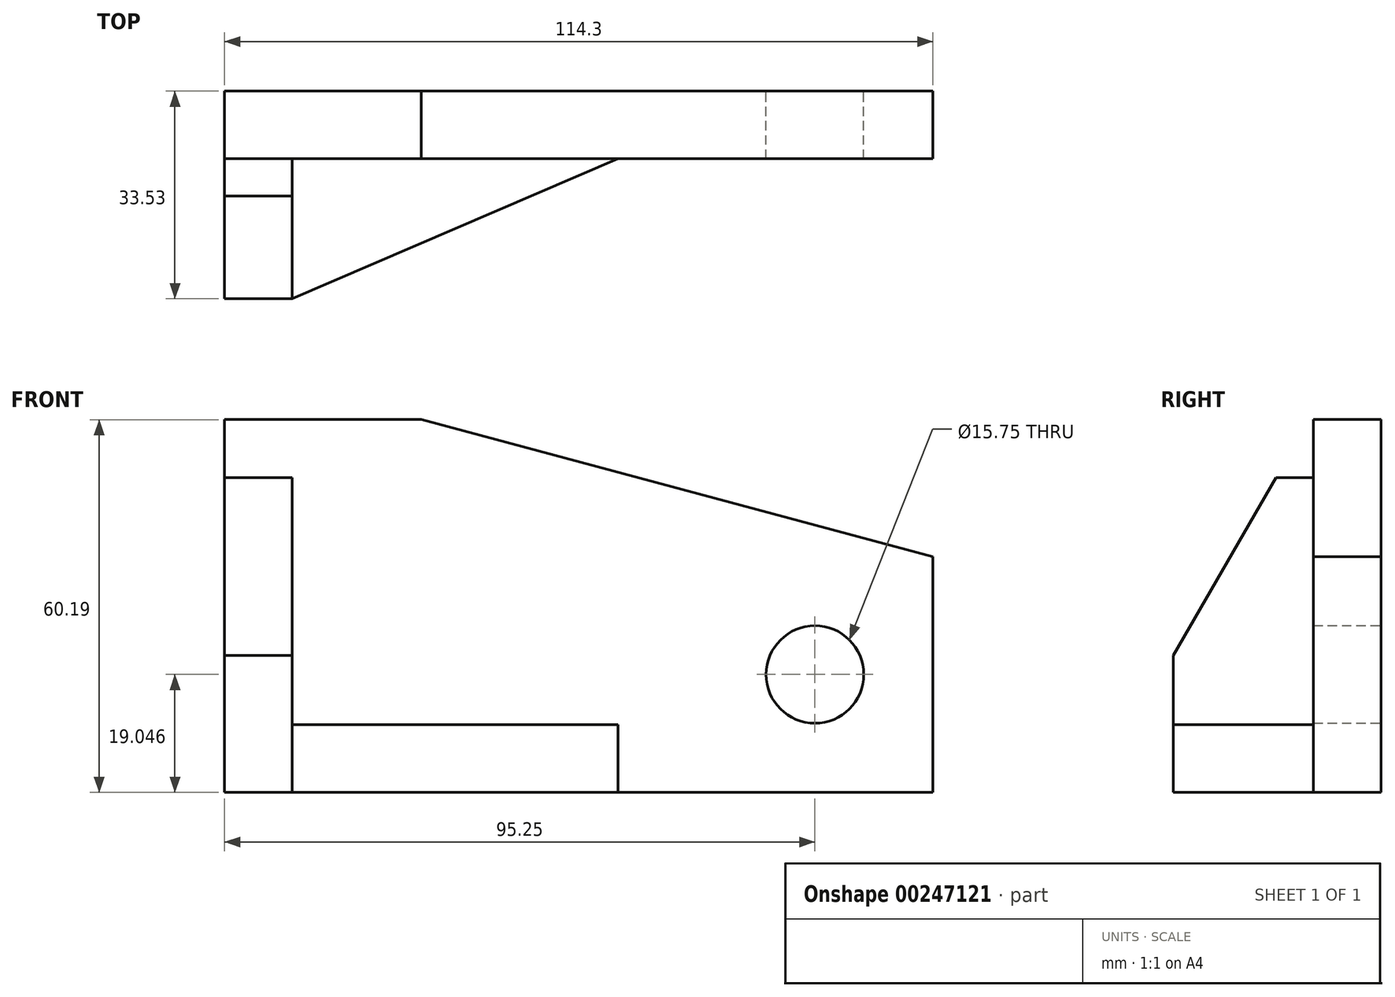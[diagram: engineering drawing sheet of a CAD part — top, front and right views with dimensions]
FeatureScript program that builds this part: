
annotation { "Feature Type Name" : "Feature", "Feature Type Description" : "" }
export const myFeature = defineFeature(function(context is Context, id is Id, definition is map)
    precondition{}
    {
        {
            var Q0;
            Q0=qCreatedBy(makeId("Front.planeOp"),FACE);
            var sketch = newSketch(context, id + "F0", { "sketchPlane" : qUnion([Q0])});
            skLineSegment(sketch, "E0", {"start": v(-63.5, -33.1) * mm, "end": v(50.8, -33.1) * mm});
            skLineSegment(sketch, "E1", {"start": v(50.8, -33.1) * mm, "end": v(50.8, 4.98) * mm});
            skLineSegment(sketch, "E2", {"start": v(-63.5, -33.1) * mm, "end": v(-63.5, 27.1) * mm});
            skLineSegment(sketch, "E3", {"start": v(-63.5, 27.1) * mm, "end": v(-31.75, 27.1) * mm});
            skLineSegment(sketch, "E4", {"start": v(-31.75, 27.1) * mm, "end": v(50.8, 4.98) * mm});
            skLineSegment(sketch, "E5", {"start": v(-31.75, 27.1) * mm, "end": v(50.8, 27.1) * mm, "construction": true});
            skLineSegment(sketch, "E6", {"start": v(50.8, 27.1) * mm, "end": v(50.8, 4.98) * mm, "construction": true});
            skLineSegment(sketch, "E7", {"start": v(-63.5, 17.7) * mm, "end": v(-52.58, 17.7) * mm});
            skLineSegment(sketch, "E8", {"start": v(-52.58, 17.7) * mm, "end": v(-52.58, -22.17) * mm});
            skLineSegment(sketch, "E9", {"start": v(-52.58, -22.17) * mm, "end": v(0, -22.17) * mm});
            skLineSegment(sketch, "E10", {"start": v(0, -22.17) * mm, "end": v(0, -33.1) * mm});
            skLineSegment(sketch, "E11", {"start": v(-52.58, -22.17) * mm, "end": v(-52.58, -33.1) * mm});
            skCircle(sketch, "E12", {"center": v(31.75, -14.04) * mm, "radius": 7.87 * mm});
            skSolve(sketch);
        }
        {
            var Q0;
            {var subQ1=sQuery(id+"F0.wireOp",EDGE,"E1");Q0=makeQuery(id+"F0.imprint","IMPRINT",FACE,{"disambiguationData":[TD([[makeQuery(id+"F0.imprint","IMPRINT",EDGE,{"derivedFrom":subQ1}),1.0]])]});}
            extrude(context, id + "F1", {"entities" : qUnion([Q0]), "depth" : 10.92 * mm});
        }
        {
            var Q0;
            {var subQ0=sQuery(id+"F0.wireOp",EDGE,"E7");Q0=makeQuery(id+"F0.imprint","IMPRINT",FACE,{"disambiguationData":[TD([[makeQuery(id+"F0.imprint","IMPRINT",EDGE,{"derivedFrom":subQ0}),-1.0]])]});}
            var Q1;
            Q1=makeQuery(id+"F0.imprint","IMPRINT",FACE,{"disambiguationData":[TD([[makeQuery(id+"F0.imprint","IMPRINT",EDGE,{"derivedFrom":sQuery(id+"F0.wireOp",EDGE,"E9")}),-1.0]])]});
            extrude(context, id + "F2", {"entities" : qUnion([Q0, Q1]), "operationType" : NewBodyOperationType.ADD, "depth" : 33.53 * mm});
        }
        {
            var Q0;
            Q0=makeQuery(id+"F2.opExtrude","CAP_EDGE",EDGE,{"disambiguationData":[OSD([sQuery(id+"F0.wireOp",EDGE,"E7")])],"isStart":false});
            chamfer(context, id + "F3", {"entities" : qUnion([Q0]), "chamferType" : ChamferType.OFFSET_ANGLE, "width" : 28.7 * mm, "oppositeDirection" : true, "angle" : 30 * degree, "tangentPropagation" : true});
        }
        {
            var Q0;
            Q0=makeQuery(id+"F2.opExtrude","SWEPT_FACE",FACE,{"disambiguationData":[OSD([sQuery(id+"F0.wireOp",EDGE,"E9")])]});
            var sketch = newSketch(context, id + "F4", { "sketchPlane" : qUnion([Q0])});
            skLineSegment(sketch, "E13", {"start": v(-52.58, -33.53) * mm, "end": v(0, -10.92) * mm});
            skSolve(sketch);
        }
        {
            var Q0;
            Q0=makeQuery(id+"F4.imprint","IMPRINT",FACE,{"disambiguationData":[TD([[makeQuery(id+"F4.imprint","IMPRINT",EDGE,{"derivedFrom":sQuery(id+"F4.wireOp",EDGE,"E13")}),-1.0]])]});
            extrude(context, id + "F5", {"entities" : qUnion([Q0]), "operationType" : NewBodyOperationType.REMOVE, "oppositeDirection" : true, "depth" : 25.4 * mm});
        }
    });
